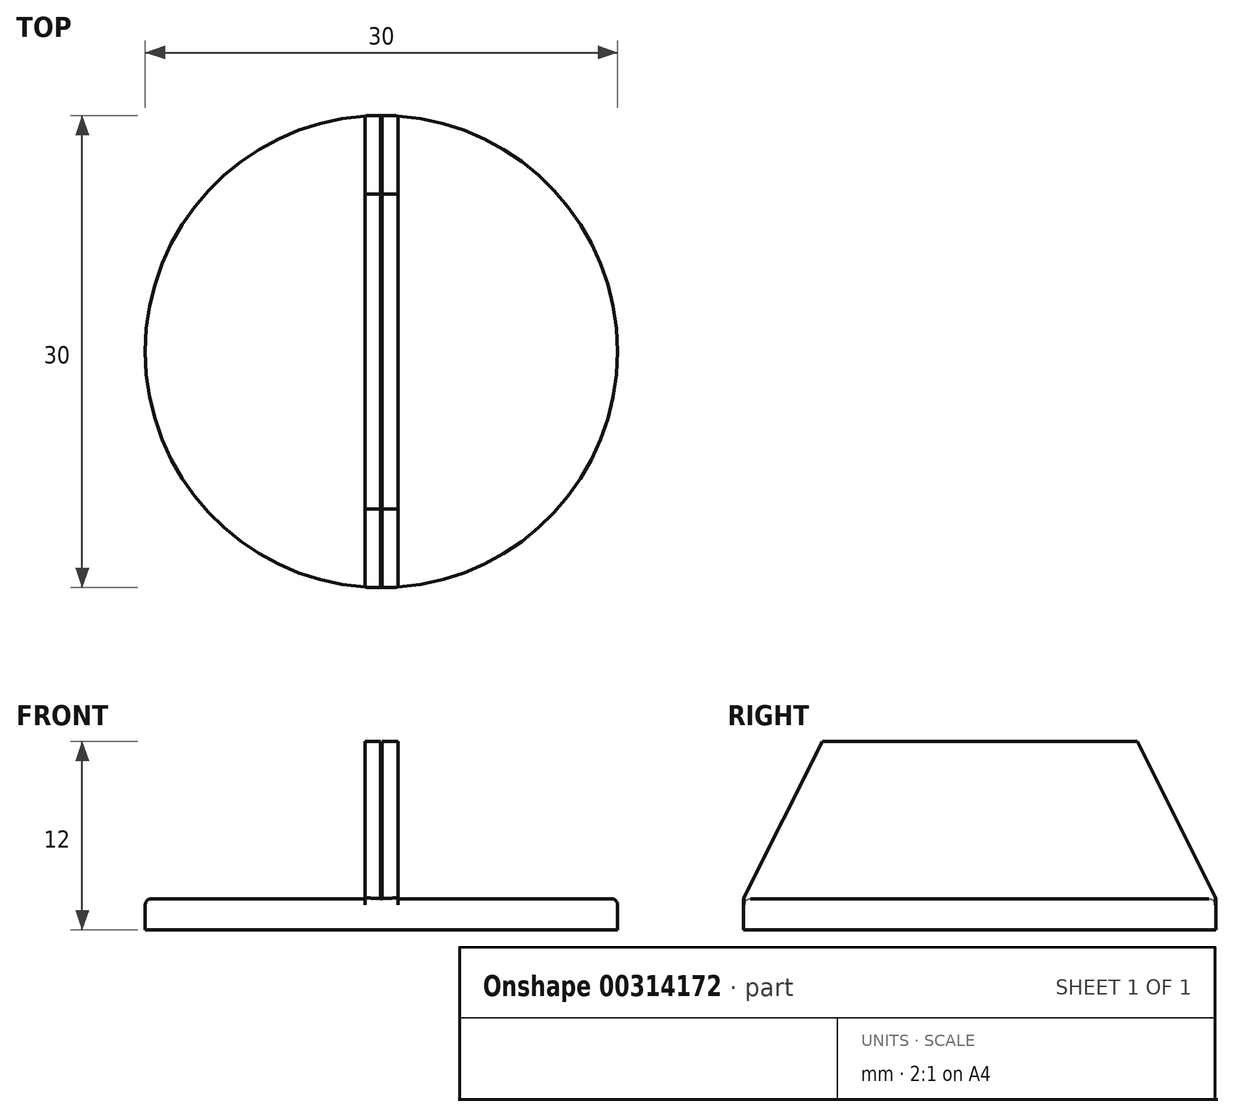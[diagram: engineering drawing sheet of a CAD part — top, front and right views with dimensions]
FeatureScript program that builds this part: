
annotation { "Feature Type Name" : "Feature", "Feature Type Description" : "" }
export const myFeature = defineFeature(function(context is Context, id is Id, definition is map)
    precondition{}
    {
        {
            var Q0;
            Q0=qCreatedBy(makeId("Top.planeOp"),FACE);
            var sketch = newSketch(context, id + "F0", { "sketchPlane" : qUnion([Q0])});
            skCircle(sketch, "E0", {"center": v(0, 0) * mm, "radius": 15 * mm});
            skCircle(sketch, "E1", {"center": v(0, 0) * mm, "radius": 19.99 * mm});
            skSolve(sketch);
        }
        {
            var Q0;
            Q0=makeQuery(id+"F0.imprint","IMPRINT",FACE,{"disambiguationData":[TD([[makeQuery(id+"F0.imprint","IMPRINT",EDGE,{"derivedFrom":sQuery(id+"F0.wireOp",EDGE,"E0")}),1.0]])]});
            extrude(context, id + "F1", {"entities" : qUnion([Q0]), "depth" : 2 * mm});
        }
        {
            var Q0;
            Q0=qCreatedBy(makeId("Right.planeOp"),FACE);
            var sketch = newSketch(context, id + "F2", { "sketchPlane" : qUnion([Q0])});
            skLineSegment(sketch, "E2.0", {"start": v(-15, 2) * mm, "end": v(15, 2) * mm});
            skLineSegment(sketch, "E3", {"start": v(15, 2) * mm, "end": v(10, 12) * mm});
            skLineSegment(sketch, "E4", {"start": v(10, 12) * mm, "end": v(-10, 12) * mm});
            skLineSegment(sketch, "E5", {"start": v(-10, 12) * mm, "end": v(-15, 2) * mm});
            skLineSegment(sketch, "E6", {"start": v(0, 0) * mm, "end": v(0, -5.15) * mm, "construction": true});
            skSolve(sketch);
        }
        {
            var Q0;
            {var subQ0=sQuery(id+"F2.wireOp",EDGE,"E3");Q0=makeQuery(id+"F2.imprint","IMPRINT",FACE,{"disambiguationData":[TD([[makeQuery(id+"F2.imprint","IMPRINT",EDGE,{"derivedFrom":subQ0}),1.0]])]});}
            extrude(context, id + "F3", {"entities" : qUnion([Q0]), "operationType" : NewBodyOperationType.ADD, "endBound" : BoundingType.SYMMETRIC, "depth" : 2.1 * mm, "hasSecondDirection" : true, "secondDirectionOppositeDirection" : true, "secondDirectionDepth" : 1.05 * mm});
        }
        {
            var Q0;
            Q0 = qSketchRegion(id + "F2", true);
            extrude(context, id + "F4", {"entities" : qUnion([Q0]), "operationType" : NewBodyOperationType.REMOVE, "endBound" : BoundingType.SYMMETRIC, "oppositeDirection" : true, "depth" : 0.1 * mm});
        }
        {
            var Q0;
            {var subQ0=sQuery(id+"F0.wireOp",EDGE,"E0");var subQ1=makeQuery(id+"F1.opExtrude","SWEPT_FACE",FACE,{"disambiguationData":[OSD([subQ0])]});var subQ2=makeQuery(id+"F1.opExtrude","CAP_FACE",FACE,{"disambiguationData":[OSD([subQ0])],"isStart":false});var subQ3=sQuery(id+"F2.wireOp",EDGE,"E2.0");Q0=makeQuery(id+"F3.boolean.opBoolean","SPLIT",EDGE,{"disambiguationData":[topologyDisambiguationEdgeConnected([subQ1,subQ2]),TD([makeQuery(id+"F3.opExtrude","CAP_FACE",FACE,{"disambiguationData":[OSD([subQ3,sQuery(id+"F2.wireOp",EDGE,"E3"),sQuery(id+"F2.wireOp",EDGE,"E4"),sQuery(id+"F2.wireOp",EDGE,"E5")])],"isStart":true})])],"derivedFrom":makeQuery(id+"F1.opExtrude","CAP_EDGE",EDGE,{"disambiguationData":[OSD([subQ0])],"isStart":false})});}
            var Q1;
            {var subQ0=sQuery(id+"F0.wireOp",EDGE,"E0");var subQ1=makeQuery(id+"F1.opExtrude","SWEPT_FACE",FACE,{"disambiguationData":[OSD([subQ0])]});var subQ2=sQuery(id+"F2.wireOp",EDGE,"E2.0");var subQ3=makeQuery(id+"F1.opExtrude","CAP_FACE",FACE,{"disambiguationData":[OSD([subQ0])],"isStart":false});Q1=makeQuery(id+"F3.boolean.opBoolean","SPLIT",EDGE,{"disambiguationData":[topologyDisambiguationEdgeConnected([subQ1,subQ3]),TD([makeQuery(id+"F3.opExtrude","CAP_FACE",FACE,{"disambiguationData":[OSD([subQ2,sQuery(id+"F2.wireOp",EDGE,"E3"),sQuery(id+"F2.wireOp",EDGE,"E4"),sQuery(id+"F2.wireOp",EDGE,"E5")])],"isStart":false})])],"derivedFrom":makeQuery(id+"F1.opExtrude","CAP_EDGE",EDGE,{"disambiguationData":[OSD([subQ0])],"isStart":false})});}
            fillet(context, id + "F5", {"entities" : qUnion([Q0, Q1]), "radius" : 0.4 * mm, "allowEdgeOverflow" : false});
        }
        {
            var Q0;
            Q0=makeQuery(id+"F0.imprint","IMPRINT",FACE,{"disambiguationData":[TD([[makeQuery(id+"F0.imprint","IMPRINT",EDGE,{"derivedFrom":sQuery(id+"F0.wireOp",EDGE,"E0")}),-1.0]])]});
            extrude(context, id + "F6", {"entities" : qUnion([Q0]), "operationType" : NewBodyOperationType.REMOVE, "depth" : 50 * mm});
        }
    });
